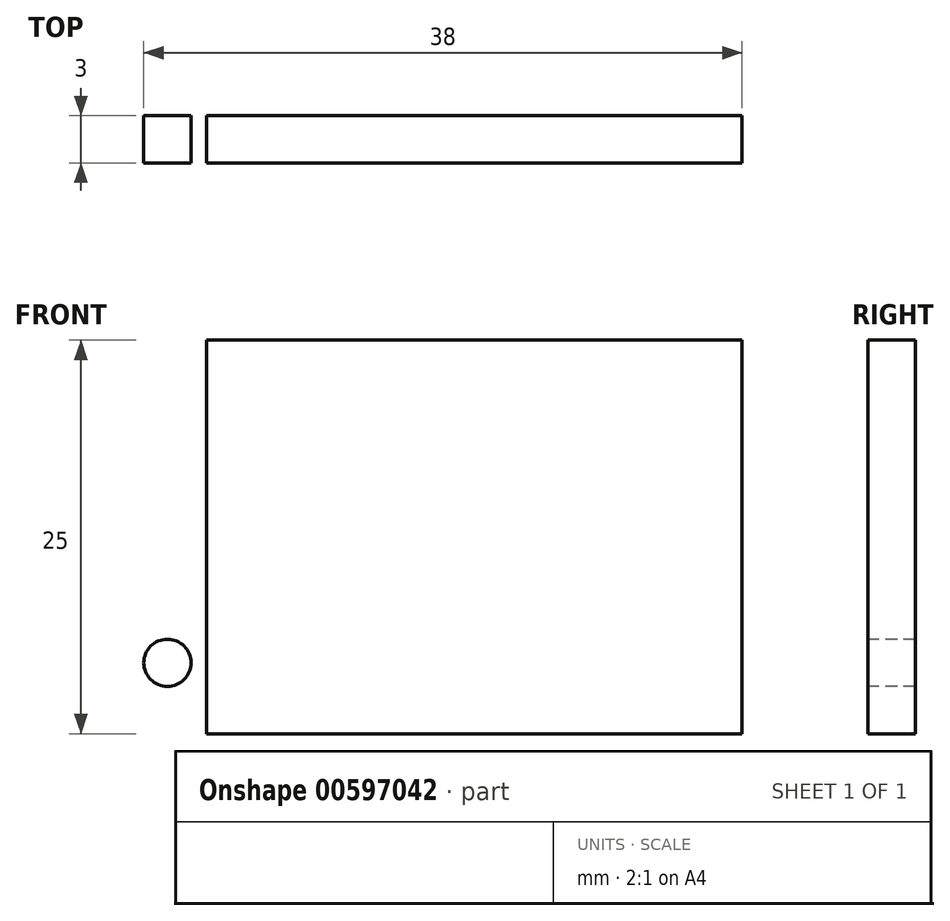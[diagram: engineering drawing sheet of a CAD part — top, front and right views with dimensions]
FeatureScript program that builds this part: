
annotation { "Feature Type Name" : "Feature", "Feature Type Description" : "" }
export const myFeature = defineFeature(function(context is Context, id is Id, definition is map)
    precondition{}
    {
        {
            var Q0;
            Q0=qCreatedBy(makeId("Top.planeOp"),FACE);
            var sketch = newSketch(context, id + "F0", { "sketchPlane" : qUnion([Q0])});
            skLineSegment(sketch, "E0.bottom", {"start": v(0, 0) * mm, "end": v(41, 0) * mm});
            skLineSegment(sketch, "E0.top", {"start": v(0, 3) * mm, "end": v(41, 3) * mm});
            skLineSegment(sketch, "E0.left", {"start": v(0, 0) * mm, "end": v(0, 3) * mm});
            skLineSegment(sketch, "E0.right", {"start": v(41, 0) * mm, "end": v(41, 3) * mm});
            skLineSegment(sketch, "E1.bottom", {"start": v(41, 3) * mm, "end": v(38, 3) * mm});
            skLineSegment(sketch, "E1.top", {"start": v(41, 10) * mm, "end": v(38, 10) * mm});
            skLineSegment(sketch, "E1.left", {"start": v(41, 3) * mm, "end": v(41, 10) * mm});
            skLineSegment(sketch, "E1.right", {"start": v(38, 3) * mm, "end": v(38, 10) * mm});
            skSolve(sketch);
        }
        {
            var Q0;
            Q0=makeQuery(id+"F0.imprint","IMPRINT",FACE,{"disambiguationData":[TD([[makeQuery(id+"F0.imprint","IMPRINT",EDGE,{"derivedFrom":sQuery(id+"F0.wireOp",EDGE,"E0.bottom")}),1.0]])]});
            var Q1;
            Q1=makeQuery(id+"F0.imprint","IMPRINT",FACE,{"disambiguationData":[TD([[makeQuery(id+"F0.imprint","IMPRINT",EDGE,{"derivedFrom":sQuery(id+"F0.wireOp",EDGE,"E1.bottom")}),-1.0]])]});
            extrude(context, id + "F1", {"entities" : qUnion([Q0, Q1]), "endBound" : BoundingType.SYMMETRIC, "depth" : 25 * mm, "offsetDistance" : 25.4 * mm});
        }
        {
            var Q0;
            Q0=makeQuery(id+"F1.opExtrude","SWEPT_FACE",FACE,{"disambiguationData":[OSD([sQuery(id+"F0.wireOp",EDGE,"E0.bottom")])]});
            var sketch = newSketch(context, id + "F2", { "sketchPlane" : qUnion([Q0])});
            skLineSegment(sketch, "E2.bottom", {"start": v(0, 12.5) * mm, "end": v(7, 12.5) * mm});
            skLineSegment(sketch, "E2.top", {"start": v(0, -12.5) * mm, "end": v(7, -12.5) * mm});
            skLineSegment(sketch, "E2.left", {"start": v(0, 12.5) * mm, "end": v(0, -12.5) * mm});
            skLineSegment(sketch, "E2.right", {"start": v(7, 12.5) * mm, "end": v(7, -12.5) * mm});
            skLineSegment(sketch, "E3", {"start": v(0, 0) * mm, "end": v(41, 0) * mm, "construction": true});
            skCircle(sketch, "E4", {"center": v(4.5, 8) * mm, "radius": 1.5 * mm});
            skCircle(sketch, "E5.MirrorC", {"center": v(4.5, -8) * mm, "radius": 1.5 * mm});
            skSolve(sketch);
        }
        {
            var Q0;
            Q0=makeQuery(id+"F2.imprint","IMPRINT",FACE,{"disambiguationData":[TD([[makeQuery(id+"F2.imprint","IMPRINT",EDGE,{"derivedFrom":sQuery(id+"F2.wireOp",EDGE,"E4")}),1.0]])]});
            var Q1;
            Q1=makeQuery(id+"F2.imprint","IMPRINT",FACE,{"disambiguationData":[TD([[makeQuery(id+"F2.imprint","IMPRINT",EDGE,{"derivedFrom":sQuery(id+"F2.wireOp",EDGE,"E5.MirrorC")}),-1.0]])]});
            extrude(context, id + "F3", {"entities" : qUnion([Q0, Q1]), "operationType" : NewBodyOperationType.REMOVE, "oppositeDirection" : true, "depth" : 25.4 * mm, "offsetDistance" : 25.4 * mm});
        }
        {
            var Q0;
            Q0=makeQuery(id+"F1.opExtrude","SWEPT_FACE",FACE,{"disambiguationData":[OSD([sQuery(id+"F0.wireOp",EDGE,"E0.right"),sQuery(id+"F0.wireOp",EDGE,"E1.left")])]});
            var sketch = newSketch(context, id + "F4", { "sketchPlane" : qUnion([Q0])});
            skLineSegment(sketch, "E6", {"start": v(0, 0) * mm, "end": v(10, 0) * mm, "construction": true});
            skCircle(sketch, "E7", {"center": v(5.5, 8) * mm, "radius": 1.5 * mm});
            skCircle(sketch, "E8.MirrorC", {"center": v(5.5, -8) * mm, "radius": 1.5 * mm});
            skSolve(sketch);
        }
        {
            var Q0;
            Q0=makeQuery(id+"F4.imprint","IMPRINT",FACE,{"disambiguationData":[TD([[makeQuery(id+"F4.imprint","IMPRINT",EDGE,{"derivedFrom":sQuery(id+"F4.wireOp",EDGE,"E7")}),1.0]])]});
            var Q1;
            Q1=makeQuery(id+"F4.imprint","IMPRINT",FACE,{"disambiguationData":[TD([[makeQuery(id+"F4.imprint","IMPRINT",EDGE,{"derivedFrom":sQuery(id+"F4.wireOp",EDGE,"E8.MirrorC")}),-1.0]])]});
            extrude(context, id + "F5", {"entities" : qUnion([Q0, Q1]), "operationType" : NewBodyOperationType.REMOVE, "oppositeDirection" : true, "depth" : 25.4 * mm, "offsetDistance" : 25.4 * mm});
        }
    });
